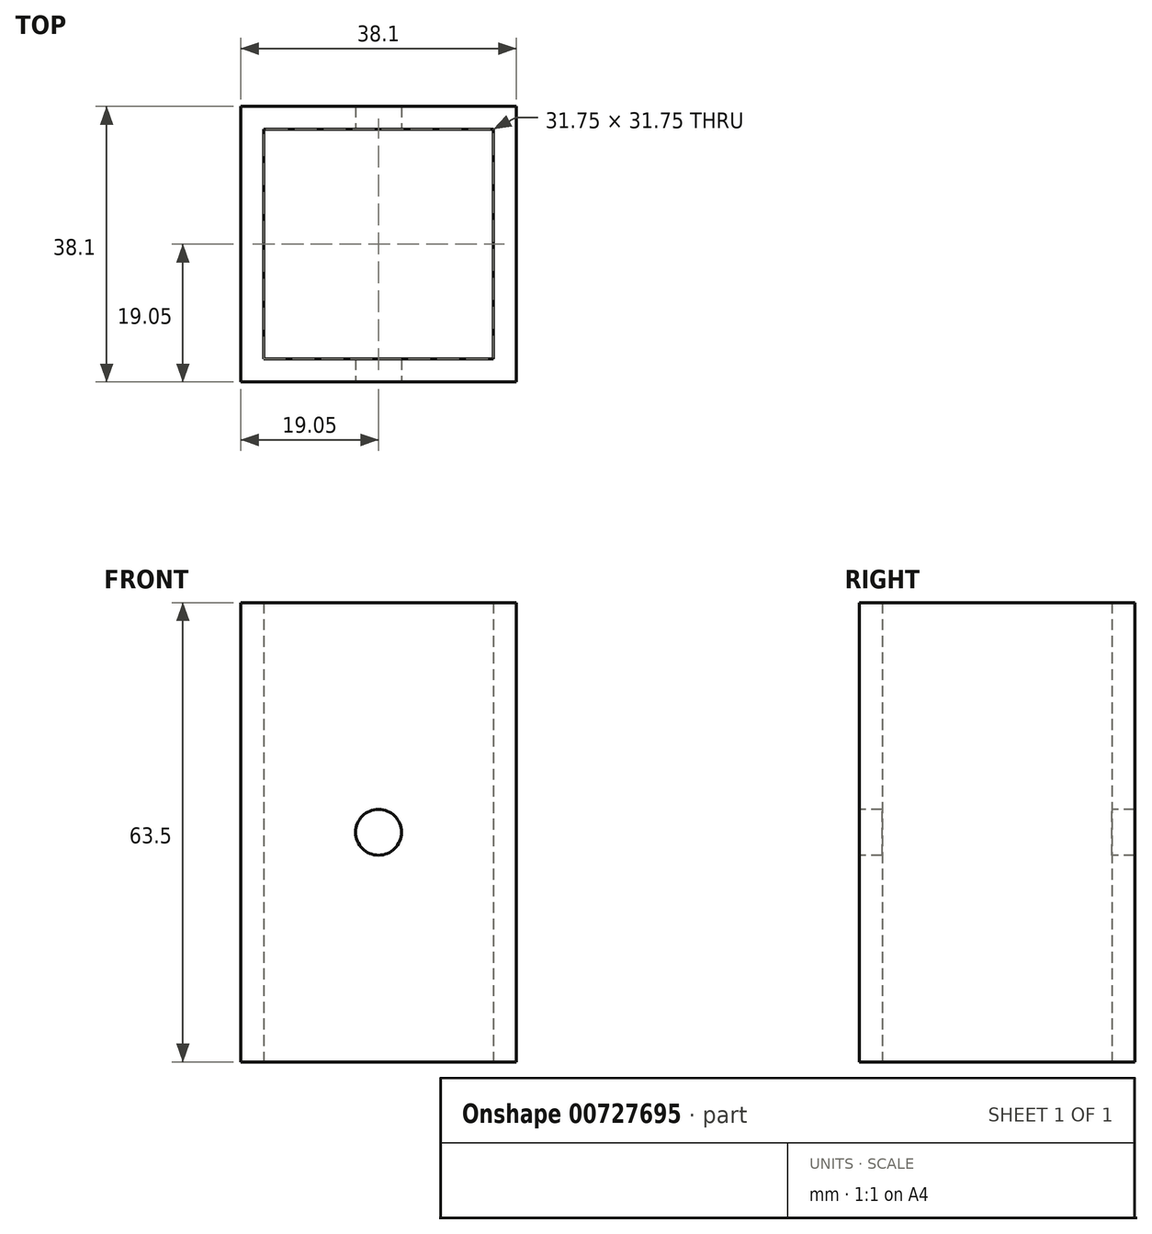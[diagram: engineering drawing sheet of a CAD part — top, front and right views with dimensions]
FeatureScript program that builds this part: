
annotation { "Feature Type Name" : "Feature", "Feature Type Description" : "" }
export const myFeature = defineFeature(function(context is Context, id is Id, definition is map)
    precondition{}
    {
        {
            var Q0;
            Q0=qCreatedBy(makeId("Top.planeOp"),FACE);
            var sketch = newSketch(context, id + "F0", { "sketchPlane" : qUnion([Q0])});
            skLineSegment(sketch, "E0.bottom", {"start": v(15.88, 15.88) * mm, "end": v(-15.88, 15.88) * mm});
            skLineSegment(sketch, "E0.top", {"start": v(15.88, -15.88) * mm, "end": v(-15.88, -15.88) * mm});
            skLineSegment(sketch, "E0.left", {"start": v(15.88, 15.88) * mm, "end": v(15.88, -15.88) * mm});
            skLineSegment(sketch, "E0.right", {"start": v(-15.88, 15.88) * mm, "end": v(-15.88, -15.88) * mm});
            skPoint(sketch, "E0.middle", {"position": v(0, 0) * mm});
            skLineSegment(sketch, "E1.0", {"start": v(19.05, -19.05) * mm, "end": v(-19.05, -19.05) * mm});
            skLineSegment(sketch, "E1.1", {"start": v(19.05, 19.05) * mm, "end": v(19.05, -19.05) * mm});
            skLineSegment(sketch, "E1.2", {"start": v(19.05, 19.05) * mm, "end": v(-19.05, 19.05) * mm});
            skLineSegment(sketch, "E1.3", {"start": v(-19.05, 19.05) * mm, "end": v(-19.05, -19.05) * mm});
            skSolve(sketch);
        }
        {
            var Q0;
            Q0 = qSketchRegion(id + "F0", true);
            extrude(context, id + "F1", {"entities" : qUnion([Q0]), "depth" : 63.5 * mm, "offsetDistance" : 25.4 * mm});
        }
        {
            var Q0;
            Q0=makeQuery(id+"F1.opExtrude","SWEPT_FACE",FACE,{"disambiguationData":[OSD([sQuery(id+"F0.wireOp",EDGE,"E1.0")])]});
            var sketch = newSketch(context, id + "F2", { "sketchPlane" : qUnion([Q0])});
            skLineSegment(sketch, "E2", {"start": v(-19.05, 63.5) * mm, "end": v(19.05, 0) * mm});
            skCircle(sketch, "E3", {"center": v(0, 31.75) * mm, "radius": 3.18 * mm});
            skSolve(sketch);
        }
        {
            var Q0;
            Q0 = qSketchRegion(id + "F2", true);
            extrude(context, id + "F3", {"entities" : qUnion([Q0]), "operationType" : NewBodyOperationType.REMOVE, "endBound" : BoundingType.THROUGH_ALL, "oppositeDirection" : true, "depth" : 25.4 * mm, "offsetDistance" : 25.4 * mm});
        }
    });
